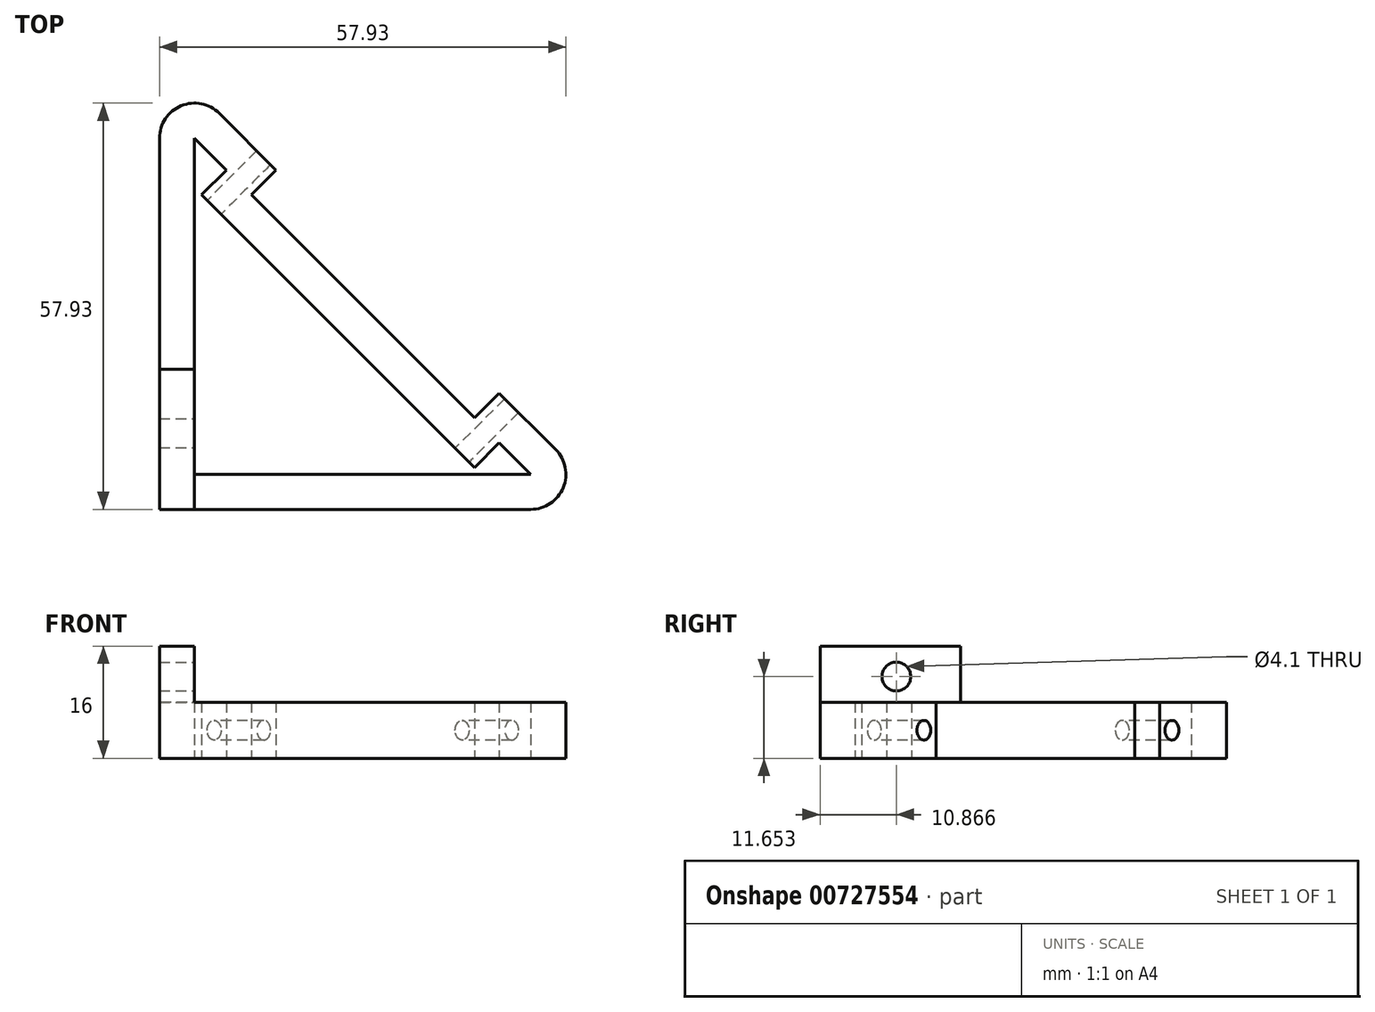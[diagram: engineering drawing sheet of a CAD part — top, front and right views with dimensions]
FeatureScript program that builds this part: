
annotation { "Feature Type Name" : "Feature", "Feature Type Description" : "" }
export const myFeature = defineFeature(function(context is Context, id is Id, definition is map)
    precondition{}
    {
        {
            var Q0;
            Q0=qCreatedBy(makeId("Top.planeOp"),FACE);
            var sketch = newSketch(context, id + "F0", { "sketchPlane" : qUnion([Q0])});
            skLineSegment(sketch, "E0", {"start": v(16.4, 9.24) * mm, "end": v(81.4, -55.76) * mm});
            skLineSegment(sketch, "E1", {"start": v(81.4, -55.76) * mm, "end": v(16.4, -55.76) * mm});
            skLineSegment(sketch, "E2", {"start": v(16.4, -55.76) * mm, "end": v(16.4, 9.24) * mm});
            skSolve(sketch);
        }
        {
            var Q0;
            Q0=makeQuery(id+"F0.imprint","IMPRINT",FACE,{"disambiguationData":[TD([[makeQuery(id+"F0.imprint","IMPRINT",EDGE,{"derivedFrom":sQuery(id+"F0.wireOp",EDGE,"E0")}),-1.0]])]});
            extrude(context, id + "F1", {"entities" : qUnion([Q0]), "depth" : 8 * mm, "offsetDistance" : 25 * mm});
        }
        {
            var Q0;
            Q0=makeQuery(id+"F1.opExtrude","SWEPT_FACE",FACE,{"disambiguationData":[OSD([sQuery(id+"F0.wireOp",EDGE,"E0")])]});
            var sketch = newSketch(context, id + "F2", { "sketchPlane" : qUnion([Q0])});
            skLineSegment(sketch, "E3", {"start": v(-5.06, 4) * mm, "end": v(-96.98, 4) * mm, "construction": true});
            skPoint(sketch, "E4", {"position": v(-26.06, 4) * mm});
            skPoint(sketch, "E5", {"position": v(-76.06, 4) * mm});
            skLineSegment(sketch, "E6.bottom", {"start": v(-28.56, 8) * mm, "end": v(-73.56, 8) * mm});
            skLineSegment(sketch, "E6.top", {"start": v(-28.56, 0) * mm, "end": v(-73.56, 0) * mm});
            skLineSegment(sketch, "E6.left", {"start": v(-28.56, 8) * mm, "end": v(-28.56, 0) * mm});
            skLineSegment(sketch, "E6.right", {"start": v(-73.56, 8) * mm, "end": v(-73.56, 0) * mm});
            skSolve(sketch);
        }
        {
            var Q0;
            Q0=qSketchRegion(id+"F2",true);
            extrude(context, id + "F3", {"entities" : qUnion([Q0]), "operationType" : NewBodyOperationType.REMOVE, "oppositeDirection" : true, "depth" : 5 * mm, "offsetDistance" : 25 * mm});
        }
        {
            var Q0;
            Q0=makeQuery(id+"F1.opExtrude","CAP_FACE",FACE,{"disambiguationData":[OSD([sQuery(id+"F0.wireOp",EDGE,"wovUUTVw-necz-sFzB-og7f-I1zAXtlkwNlU"),sQuery(id+"F0.wireOp",EDGE,"E0"),sQuery(id+"F0.wireOp",EDGE,"E1"),sQuery(id+"F0.wireOp",EDGE,"E2"),sQuery(id+"F0.wireOp",EDGE,"JPAwPART-SAmD-cNFy-OBPy-EqJGHYJ7Oe2y"),sQuery(id+"F0.wireOp",EDGE,"gEYzRGeL-rZ4c-56CZ-83J1-QYXdiLNEjnBU")])],"isStart":false});
            var Q1;
            Q1=makeQuery(id+"F1.opExtrude","CAP_FACE",FACE,{"disambiguationData":[OSD([sQuery(id+"F0.wireOp",EDGE,"wovUUTVw-necz-sFzB-og7f-I1zAXtlkwNlU"),sQuery(id+"F0.wireOp",EDGE,"E0"),sQuery(id+"F0.wireOp",EDGE,"E1"),sQuery(id+"F0.wireOp",EDGE,"E2"),sQuery(id+"F0.wireOp",EDGE,"JPAwPART-SAmD-cNFy-OBPy-EqJGHYJ7Oe2y"),sQuery(id+"F0.wireOp",EDGE,"gEYzRGeL-rZ4c-56CZ-83J1-QYXdiLNEjnBU")])],"isStart":true});
            shell(context, id + "F4", {"entities" : qUnion([Q0, Q1]), "thickness" : 5 * mm});
        }
        {
            var Q0;
            Q0=sQuery(id+"F2.wireOp",VERTEX,"E4");
            var Q1;
            Q1=sQuery(id+"F2.wireOp",VERTEX,"E5");
            var Q2;
            Q2=makeQuery(id+"F1.opExtrude","SWEPT_BODY",BODY,{"disambiguationData":[OSD([sQuery(id+"F0.wireOp",EDGE,"wovUUTVw-necz-sFzB-og7f-I1zAXtlkwNlU"),sQuery(id+"F0.wireOp",EDGE,"E0"),sQuery(id+"F0.wireOp",EDGE,"E1"),sQuery(id+"F0.wireOp",EDGE,"E2"),sQuery(id+"F0.wireOp",EDGE,"JPAwPART-SAmD-cNFy-OBPy-EqJGHYJ7Oe2y"),sQuery(id+"F0.wireOp",EDGE,"gEYzRGeL-rZ4c-56CZ-83J1-QYXdiLNEjnBU")])]});
            hole(context, id + "F5", {"style" : HoleStyle.SIMPLE, "endStyle" : HoleEndStyle.BLIND, "holeDiameter" : 2.8 * mm, "majorDiameter" : 5 * mm, "holeDepth" : 11 * mm, "tappedDepth" : 30 * mm, "tapClearance" : 3, "startFromSketch" : true, "locations" : qUnion([Q0, Q1]), "scope" : qUnion([Q2])});
        }
        {
            var Q0;
            Q0=makeQuery(id+"F1.opExtrude","CAP_FACE",FACE,{"disambiguationData":[OSD([sQuery(id+"F0.wireOp",EDGE,"wovUUTVw-necz-sFzB-og7f-I1zAXtlkwNlU"),sQuery(id+"F0.wireOp",EDGE,"E0"),sQuery(id+"F0.wireOp",EDGE,"E1"),sQuery(id+"F0.wireOp",EDGE,"E2"),sQuery(id+"F0.wireOp",EDGE,"JPAwPART-SAmD-cNFy-OBPy-EqJGHYJ7Oe2y"),sQuery(id+"F0.wireOp",EDGE,"gEYzRGeL-rZ4c-56CZ-83J1-QYXdiLNEjnBU")])],"isStart":false});
            var sketch = newSketch(context, id + "F6", { "sketchPlane" : qUnion([Q0])});
            skLineSegment(sketch, "E7.bottom", {"start": v(16.4, -35.76) * mm, "end": v(21.4, -35.76) * mm});
            skLineSegment(sketch, "E7.top", {"start": v(16.4, -55.76) * mm, "end": v(21.4, -55.76) * mm});
            skLineSegment(sketch, "E7.left", {"start": v(16.4, -35.76) * mm, "end": v(16.4, -55.76) * mm});
            skLineSegment(sketch, "E7.right", {"start": v(21.4, -35.76) * mm, "end": v(21.4, -55.76) * mm});
            skSolve(sketch);
        }
        {
            var Q0;
            {var subQ5=sQuery(id+"F6.wireOp",EDGE,"E7.bottom");Q0=makeQuery(id+"F6.imprint","IMPRINT",FACE,{"disambiguationData":[TD([[makeQuery(id+"F6.imprint","IMPRINT",EDGE,{"derivedFrom":subQ5}),-1.0]])]});}
            extrude(context, id + "F7", {"entities" : qUnion([Q0]), "operationType" : NewBodyOperationType.ADD, "depth" : 8 * mm, "offsetDistance" : 25 * mm});
        }
        {
            var Q0;
            Q0=makeQuery(id+"F7.boolean.opBoolean","MERGE",FACE,{"derivedFrom":[makeQuery(id+"F1.opExtrude","SWEPT_FACE",FACE,{"disambiguationData":[OSD([sQuery(id+"F0.wireOp",EDGE,"E2")])]}),makeQuery(id+"F7.opExtrude","SWEPT_FACE",FACE,{"disambiguationData":[OSD([sQuery(id+"F6.wireOp",EDGE,"E7.left")])]})]});
            var sketch = newSketch(context, id + "F8", { "sketchPlane" : qUnion([Q0])});
            skLineSegment(sketch, "E8", {"start": v(35.76, 8) * mm, "end": v(55.76, 16) * mm, "construction": true});
            skPoint(sketch, "E9", {"position": v(44.9, 11.65) * mm});
            skSolve(sketch);
        }
        {
            var Q0;
            Q0=sQuery(id+"F8.wireOp",VERTEX,"E9");
            var Q1;
            Q1=makeQuery(id+"F1.opExtrude","SWEPT_BODY",BODY,{"disambiguationData":[OSD([sQuery(id+"F0.wireOp",EDGE,"wovUUTVw-necz-sFzB-og7f-I1zAXtlkwNlU"),sQuery(id+"F0.wireOp",EDGE,"E0"),sQuery(id+"F0.wireOp",EDGE,"E1"),sQuery(id+"F0.wireOp",EDGE,"E2"),sQuery(id+"F0.wireOp",EDGE,"JPAwPART-SAmD-cNFy-OBPy-EqJGHYJ7Oe2y"),sQuery(id+"F0.wireOp",EDGE,"gEYzRGeL-rZ4c-56CZ-83J1-QYXdiLNEjnBU")])]});
            hole(context, id + "F9", {"style" : HoleStyle.SIMPLE, "endStyle" : HoleEndStyle.BLIND, "holeDiameter" : 4.1 * mm, "majorDiameter" : 5 * mm, "holeDepth" : 7 * mm, "tappedDepth" : 30 * mm, "tapClearance" : 3, "startFromSketch" : true, "locations" : qUnion([Q0]), "scope" : qUnion([Q1])});
        }
        {
            var Q0;
            Q0=makeQuery(id+"F1.opExtrude","SWEPT_EDGE",EDGE,{"disambiguationData":[OSD([sQuery(id+"F0.wireOp",EDGE,"E0"),sQuery(id+"F0.wireOp",EDGE,"E2")])]});
            var Q1;
            Q1=makeQuery(id+"F1.opExtrude","SWEPT_EDGE",EDGE,{"disambiguationData":[OSD([sQuery(id+"F0.wireOp",EDGE,"E0"),sQuery(id+"F0.wireOp",EDGE,"E1")])]});
            fillet(context, id + "F10", {"entities" : qUnion([Q0, Q1]), "radius" : 5 * mm, "tangentPropagation" : true, "allowEdgeOverflow" : false});
        }
    });
